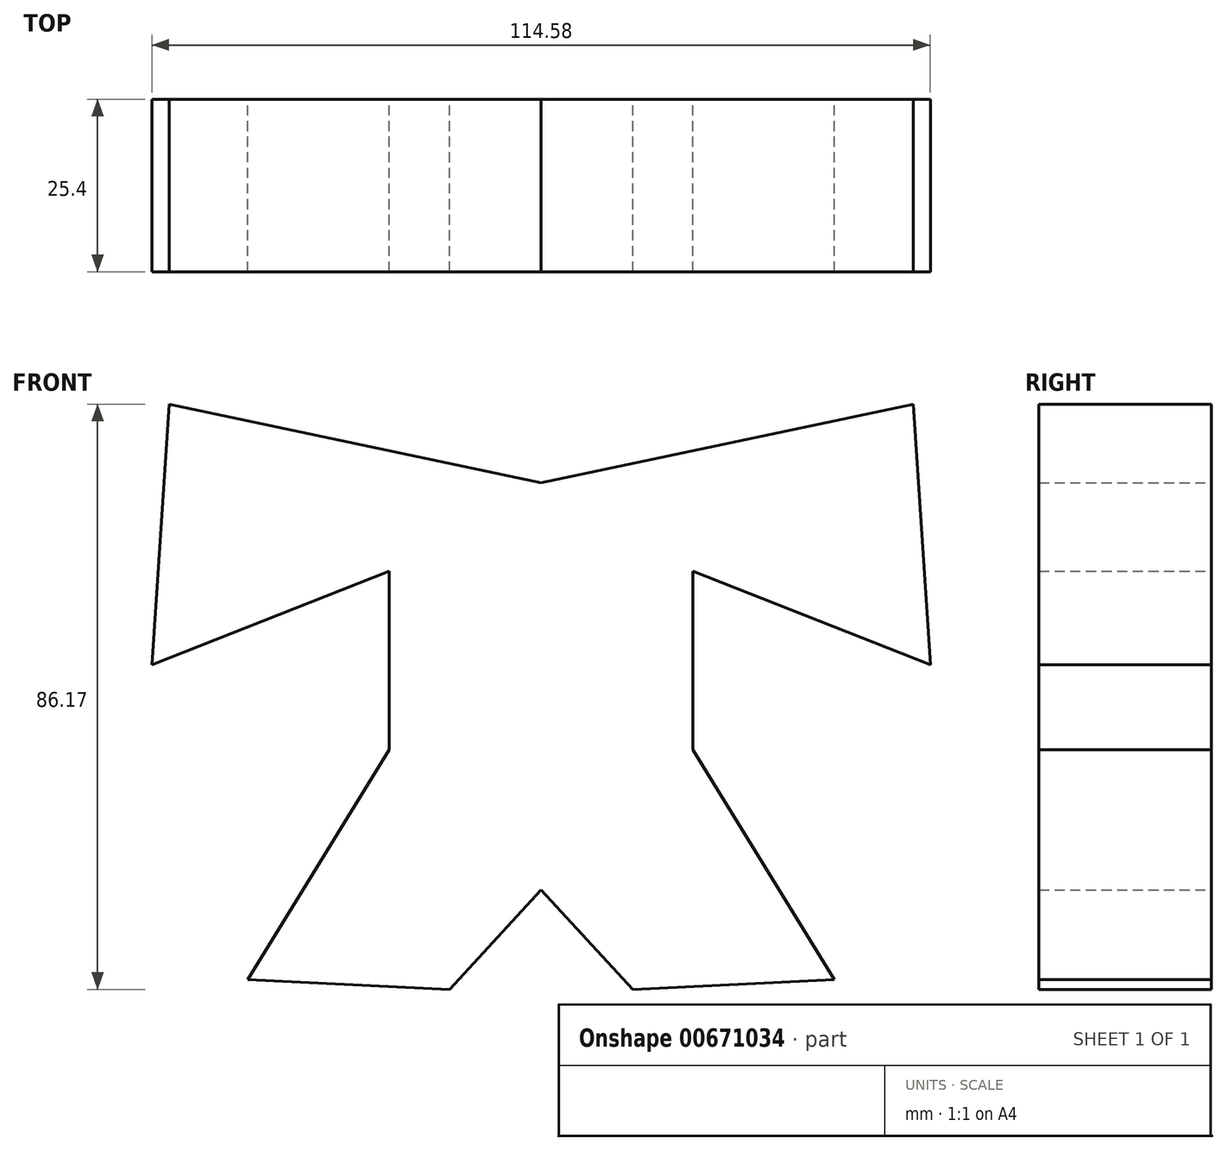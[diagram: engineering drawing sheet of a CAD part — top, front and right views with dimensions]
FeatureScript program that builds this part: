
annotation { "Feature Type Name" : "Feature", "Feature Type Description" : "" }
export const myFeature = defineFeature(function(context is Context, id is Id, definition is map)
    precondition{}
    {
        {
            var Q0;
            Q0=qCreatedBy(makeId("Front.planeOp"),FACE);
            var sketch = newSketch(context, id + "F0", { "sketchPlane" : qUnion([Q0])});
            skLineSegment(sketch, "E0", {"start": v(0, 52.22) * mm, "end": v(-54.76, 63.8) * mm});
            skLineSegment(sketch, "E1", {"start": v(-54.76, 63.8) * mm, "end": v(-57.3, 25.43) * mm});
            skLineSegment(sketch, "E2", {"start": v(-57.3, 25.43) * mm, "end": v(-22.36, 39.2) * mm});
            skLineSegment(sketch, "E3", {"start": v(-22.36, 39.2) * mm, "end": v(-22.36, 12.94) * mm});
            skLineSegment(sketch, "E4", {"start": v(-22.36, 12.94) * mm, "end": v(-43.17, -20.9) * mm});
            skLineSegment(sketch, "E5", {"start": v(-43.17, -20.9) * mm, "end": v(-13.49, -22.36) * mm});
            skLineSegment(sketch, "E6", {"start": v(-13.49, -22.36) * mm, "end": v(0, -7.7) * mm});
            skLineSegment(sketch, "E7.MirrorCS", {"start": v(0, 52.22) * mm, "end": v(54.76, 63.8) * mm});
            skLineSegment(sketch, "E8.MirrorCS", {"start": v(54.76, 63.8) * mm, "end": v(57.3, 25.43) * mm});
            skLineSegment(sketch, "E9.MirrorCS", {"start": v(57.3, 25.43) * mm, "end": v(22.36, 39.2) * mm});
            skLineSegment(sketch, "E10.MirrorCS", {"start": v(22.36, 39.2) * mm, "end": v(22.36, 12.94) * mm});
            skLineSegment(sketch, "E11.MirrorCS", {"start": v(22.36, 12.94) * mm, "end": v(43.17, -20.9) * mm});
            skLineSegment(sketch, "E12.MirrorCS", {"start": v(43.17, -20.9) * mm, "end": v(13.49, -22.36) * mm});
            skLineSegment(sketch, "E13.MirrorCS", {"start": v(13.49, -22.36) * mm, "end": v(0, -7.7) * mm});
            skSolve(sketch);
        }
        {
            var Q0;
            Q0=makeQuery(id+"F0.imprint","IMPRINT",FACE,{"disambiguationData":[TD([[makeQuery(id+"F0.imprint","IMPRINT",EDGE,{"derivedFrom":sQuery(id+"F0.wireOp",EDGE,"E0")}),1.0]])]});
            extrude(context, id + "F1", {"entities" : qUnion([Q0]), "depth" : 25.4 * mm, "offsetDistance" : 25.4 * mm});
        }
    });
